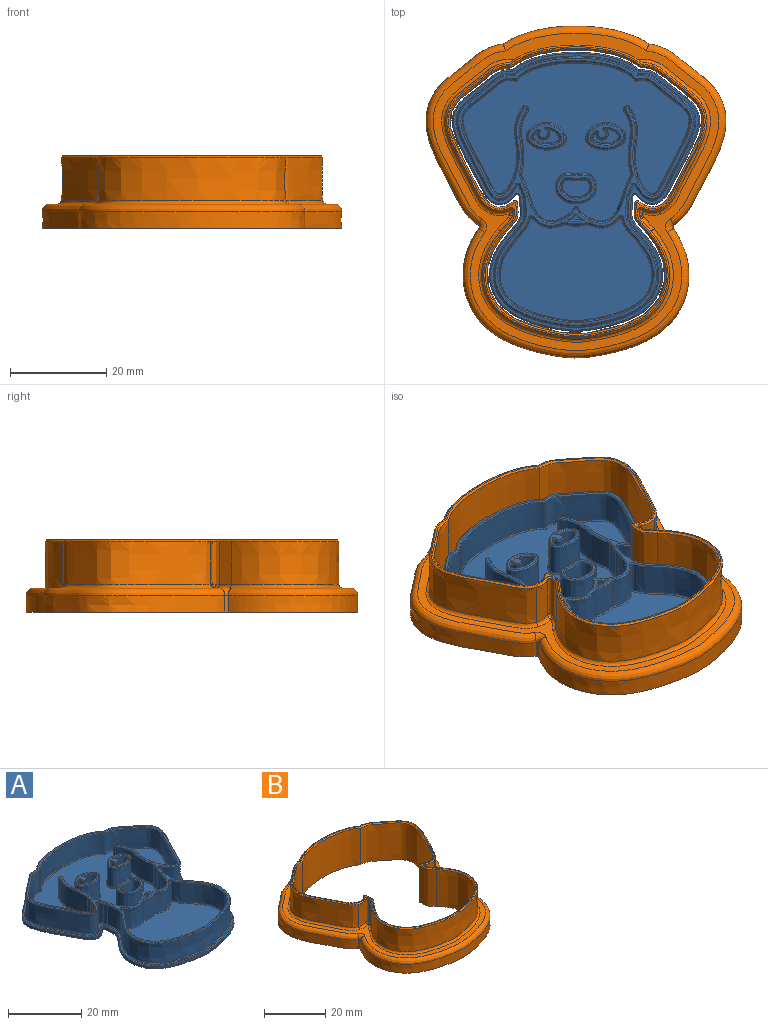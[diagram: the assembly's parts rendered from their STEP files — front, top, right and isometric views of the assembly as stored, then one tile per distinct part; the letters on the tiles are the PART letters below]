
ASSEMBLY  parts=2 mates=1
PART A: 217 faces, bbox 51.8x58.5x8.3 mm
  f0: plane 47x32.89mm, normal (0,0,1), area 914.6mm2, adj f103,f104,f105,f106,f107,f108,f109,f110
  f1: plane 57.65x51.01mm, normal (0,0,1), area 99.7mm2, adj f93,f94,f95,f96,f97,f98,f99,f100
  f2: plane 0.75x0.22mm, normal (0.92,-0.39,0), area 0.2mm2, adj f7,f8,f77,f93
  f3: extruded ~28.07x13.13mm, area 31.7mm2, adj f8,f77,f79,f96
  f4: extruded ~26.17x3.56mm, area 20.7mm2, adj f8,f79,f80,f100
  f5: extruded ~28.07x13.13mm, area 31.7mm2, adj f8,f78,f80,f101
  f6: plane 0.75x0.23mm, normal (-0.92,-0.39,0), area 0.2mm2, adj f7,f8,f78,f97
  f7: extruded ~35.85x28.04mm, area 62.9mm2, adj f2,f6,f8,f95
  f8: plane 58.16x51.5mm, normal (0,0,-1), area 2076.8mm2, adj f2,f3,f4,f5,f6,f7,f77,f78
  f9: extruded ~6.75x1.14mm, area 10.1mm2, adj f10,f47,f49,f215
  f10: extruded ~6.75x2.28mm, area 15.4mm2, adj f9,f47,f49,f216
  f11: extruded ~6.5x4.94mm, area 32.5mm2, adj f12,f44,f147,f199
  f12: extruded ~6.54x6.5mm, area 47.4mm2, adj f11,f65,f149,f201
  f13: extruded ~32.03x21.55mm, area 445.9mm2, adj f65,f66,f148,f198
  f14: extruded ~33.88x27.04mm, area 525.8mm2, adj f15,f45,f138,f166
  f15: extruded ~6.5x1.13mm, area 7.8mm2, adj f14,f16,f136,f168
  f16: plane 6.5x1.24mm, normal (0.92,-0.39,0), area 8.8mm2, adj f15,f74,f134,f167
  f17: extruded ~6.5x0.39mm, area 2.9mm2, adj f18,f74,f131,f163
  f18: extruded ~26.04x12.06mm, area 257.6mm2, adj f17,f70,f133,f161
  f19: extruded ~25.4x6.5mm, area 175.4mm2, adj f70,f73,f137,f157
  f20: extruded ~26.04x12.07mm, area 257.6mm2, adj f21,f73,f141,f156
  f21: extruded ~6.5x0.39mm, area 2.9mm2, adj f20,f67,f143,f158
  f22: plane 6.5x1.24mm, normal (-0.92,-0.39,0), area 8.8mm2, adj f45,f67,f142,f162
  f23: extruded ~13.41x6.5mm, area 89.6mm2, adj f24,f75,f124,f176
  f24: plane 6.5x3.07mm, normal (-0.92,0.39,0), area 21.7mm2, adj f23,f25,f122,f174
  f25: extruded ~6.5x1.35mm, area 9.3mm2, adj f24,f26,f120,f172
  f26: extruded ~7.32x6.5mm, area 68.8mm2, adj f25,f27,f118,f170
  f27: extruded ~6.5x2.18mm, area 18.7mm2, adj f26,f28,f116,f169
  f28: extruded ~6.75x1.66mm, area 7.6mm2, adj f27,f29,f48,f114,f169,f171
  f29: extruded ~6.5x2.23mm, area 19.1mm2, adj f28,f30,f112,f171
  f30: extruded ~7.28x6.5mm, area 68.5mm2, adj f29,f31,f110,f173
  f31: extruded ~6.5x1.35mm, area 9.3mm2, adj f30,f32,f108,f175
  f32: plane 6.5x3.09mm, normal (0.92,0.39,0), area 21.8mm2, adj f31,f33,f106,f177
  f33: extruded ~13.39x6.5mm, area 89.5mm2, adj f32,f69,f104,f179
  f34: plane 6.5x0.17mm, normal (0.56,0.83,0), area 1.3mm2, adj f68,f69,f105,f183
  f35: extruded ~12.37x6.5mm, area 82.8mm2, adj f36,f68,f109,f187
  f36: extruded ~6.5x1.63mm, area 10.9mm2, adj f35,f37,f111,f189
  f37: extruded ~6.5x1.34mm, area 9.3mm2, adj f36,f38,f113,f191
  f38: extruded ~24.06x11.06mm, area 238.1mm2, adj f37,f72,f115,f193
  f39: extruded ~24.57x6.5mm, area 171mm2, adj f71,f72,f119,f194
  f40: extruded ~24.06x11.06mm, area 238mm2, adj f41,f71,f123,f190
  f41: extruded ~6.5x1.33mm, area 9.3mm2, adj f40,f42,f125,f188
  f42: extruded ~6.5x1.62mm, area 10.8mm2, adj f41,f43,f127,f186
  f43: extruded ~12.4x6.5mm, area 83mm2, adj f42,f76,f129,f184
  f44: extruded ~6.5x6.5mm, area 47.1mm2, adj f11,f66,f145,f197
  f45: extruded ~6.5x1.14mm, area 7.9mm2, adj f14,f22,f140,f164
  f46: plane 6.5x0.17mm, normal (-0.56,0.83,0), area 1.3mm2, adj f75,f76,f128,f180
  f47: extruded ~6.75x1.14mm, area 10.1mm2, adj f9,f10,f49,f214
  f48: plane 55.97x49.58mm, normal (0,0,1), area 154.2mm2, adj f28,f155,f156,f157,f158,f159,f160,f161
  f49: plane 2.28x1.05mm, normal (0,0,1), area 1.1mm2, adj f9,f10,f47
  f50: plane 31.57x21.39mm, normal (0,0,1), area 515.5mm2, adj f145,f146,f147,f148,f149,f150
  f51: extruded ~6.5x5.87mm, area 83.3mm2, adj f81,f82,f90,f209
  f52: cylinder r=1.08mm len=6.5mm, axis (0,0,-1), area 33.4mm2, adj f81,f82,f91,f208
  f53: extruded ~7.86x6.5mm, area 134.7mm2, adj f154,f211
  f54: plane 7.73x5.2mm, normal (0,0,1), area 10.7mm2, adj f207,f208,f209,f210,f211
  f55: plane 5.38x2.79mm, normal (0,0,1), area 6.5mm2, adj f90,f91
  f56: extruded ~6.5x5.86mm, area 82mm2, adj f83,f84,f86,f204
  f57: extruded ~7.86x6.5mm, area 134.7mm2, adj f153,f206
  f58: cylinder r=1.08mm len=6.5mm, axis (0,0,-1), area 31.8mm2, adj f83,f84,f87,f203
  f59: plane 7.78x5.2mm, normal (0,0,1), area 11.4mm2, adj f202,f203,f204,f205,f206
  f60: plane 5.38x2.8mm, normal (0,0,1), area 6.7mm2, adj f86,f87
  f61: extruded ~6.5x6.19mm, area 110.4mm2, adj f152,f212
  f62: extruded ~8.19x6.5mm, area 150.2mm2, adj f151,f213
  f63: plane 8.04x5.85mm, normal (0,0,1), area 10.1mm2, adj f212,f213
  f64: plane 5.71x3.47mm, normal (0,0,1), area 16.4mm2, adj f152
  f65: cylinder r=0.4mm len=6.5mm, axis (0,0,-1), area 6mm2, adj f12,f13,f150,f200
  f66: cylinder r=0.4mm len=6.5mm, axis (0,0,-1), area 5.9mm2, adj f13,f44,f146,f196
  f67: cylinder r=0.4mm len=6.5mm, axis (0,0,-1), area 5.9mm2, adj f21,f22,f144,f160
  f68: cylinder r=0.4mm len=6.5mm, axis (0,0,-1), area 4.2mm2, adj f34,f35,f107,f185
  f69: cylinder r=0.4mm len=6.5mm, axis (0,0,-1), area 4mm2, adj f33,f34,f103,f181
  f70: cylinder r=0.4mm len=6.5mm, axis (0,0,-1), area 2.4mm2, adj f18,f19,f135,f159
  f71: cylinder r=0.4mm len=6.5mm, axis (0,0,-1), area 2.9mm2, adj f39,f40,f121,f192
  f72: cylinder r=0.4mm len=6.5mm, axis (0,0,-1), area 2.9mm2, adj f38,f39,f117,f195
  f73: cylinder r=0.4mm len=6.5mm, axis (0,0,-1), area 2.4mm2, adj f19,f20,f139,f155
  f74: cylinder r=0.4mm len=6.5mm, axis (0,0,-1), area 5.9mm2, adj f16,f17,f132,f165
  f75: cylinder r=0.4mm len=6.5mm, axis (0,0,-1), area 4mm2, adj f23,f46,f126,f178
  f76: cylinder r=0.4mm len=6.5mm, axis (0,0,-1), area 4.2mm2, adj f43,f46,f130,f182
  f77: cylinder r=0.4mm len=0.75mm, axis (0,0,-1), area 0.6mm2, adj f2,f3,f8,f94
  f78: cylinder r=0.4mm len=0.75mm, axis (0,0,-1), area 0.6mm2, adj f5,f6,f8,f99
  f79: cylinder r=0.4mm len=0.75mm, axis (0,0,-1), area 0.2mm2, adj f3,f4,f8,f98
  f80: cylinder r=0.4mm len=0.75mm, axis (0,0,-1), area 0.2mm2, adj f4,f5,f8,f102
  f81: cylinder r=0.1mm len=6.5mm, axis (0,0,-1), area 1.7mm2, adj f51,f52,f92,f210
  f82: cylinder r=0.1mm len=6.5mm, axis (0,0,-1), area 1.7mm2, adj f51,f52,f89,f207
  f83: cylinder r=0.1mm len=6.5mm, axis (0,0,-1), area 1.7mm2, adj f56,f58,f88,f205
  f84: cylinder r=0.1mm len=6.5mm, axis (0,0,-1), area 1.7mm2, adj f56,f58,f85,f202
  f85: bspline ~0.65x0.41mm, area 0.1mm2, adj f84,f86,f87
  f86: bspline ~5.88x3.32mm, area 4.6mm2, adj f56,f60,f85,f88
  f87: torus R=1.33mm, axis (0,0,1), area 1.9mm2, adj f58,f60,f85,f88
  f88: bspline ~0.79x0.29mm, area 0.1mm2, adj f83,f86,f87
  f89: bspline ~0.6x0.57mm, area 0.1mm2, adj f82,f90,f91
  f90: bspline ~5.88x3.31mm, area 4.6mm2, adj f51,f55,f89,f92
  f91: torus R=1.33mm, axis (0,0,1), area 2mm2, adj f52,f55,f89,f92
  f92: bspline ~0.83x0.3mm, area 0.1mm2, adj f81,f90,f91
  f93: cylinder r=0.25mm len=0.36mm, axis (-0.39,-0.92,0), area 0.1mm2, adj f1,f2,f94,f95
  f94: torus R=0.65mm, axis (0,0,1), area 0.4mm2, adj f1,f77,f93,f96
  f95: bspline ~36.08x29.88mm, area 32.9mm2, adj f1,f7,f93,f97
  f96: bspline ~28.11x13.67mm, area 16.4mm2, adj f1,f3,f94,f98
  f97: cylinder r=0.25mm len=0.36mm, axis (-0.39,0.92,0), area 0.1mm2, adj f1,f6,f95,f99
  f98: torus R=0.65mm, axis (0,0,1), area 0.2mm2, adj f1,f79,f96,f100
  f99: torus R=0.65mm, axis (0,0,1), area 0.4mm2, adj f1,f78,f97,f101
  f100: bspline ~26.62x3.96mm, area 10.8mm2, adj f1,f4,f98,f102
  f101: bspline ~28.1x13.67mm, area 16.4mm2, adj f1,f5,f99,f102
  f102: torus R=0.65mm, axis (0,0,1), area 0.2mm2, adj f1,f80,f100,f101
  f103: torus R=0.65mm, axis (0,0,1), area 0.3mm2, adj f0,f69,f104,f105
  f104: bspline ~14.22x2.05mm, area 5.4mm2, adj f0,f33,f103,f106
  f105: cylinder r=0.25mm len=0.32mm, axis (0.83,-0.56,0), area 0.1mm2, adj f0,f34,f103,f107
  f106: cylinder r=0.25mm len=3.18mm, axis (0.39,-0.92,0), area 1.3mm2, adj f0,f32,f104,f108
  f107: torus R=0.65mm, axis (0,0,1), area 0.3mm2, adj f0,f68,f105,f109
  f108: bspline ~1.91x0.87mm, area 0.6mm2, adj f0,f31,f106,f110
  f109: bspline ~15.66x2.35mm, area 5mm2, adj f0,f35,f107,f111
  f110: bspline ~8.29x6.32mm, area 4.1mm2, adj f0,f30,f108,f112
  f111: bspline ~2.23x0.77mm, area 0.7mm2, adj f0,f36,f109,f113
  f112: bspline ~6.55x4.18mm, area 1.1mm2, adj f0,f29,f110,f114
  f113: bspline ~1.88x0.92mm, area 0.6mm2, adj f0,f37,f111,f115
  f114: bspline ~1.31x0.91mm, area 0.5mm2, adj f0,f28,f112,f116
  f115: bspline ~24.1x12.37mm, area 14.2mm2, adj f0,f38,f113,f117
  f116: bspline ~2.98x2.35mm, area 1.1mm2, adj f0,f27,f114,f118
  f117: torus R=0.65mm, axis (0,0,1), area 0.2mm2, adj f0,f72,f115,f119
  f118: bspline ~10.84x7.11mm, area 4.1mm2, adj f0,f26,f116,f120
  f119: bspline ~24.99x4.07mm, area 10.3mm2, adj f0,f39,f117,f121
  f120: bspline ~1.91x0.87mm, area 0.6mm2, adj f0,f25,f118,f122
  f121: torus R=0.65mm, axis (0,0,1), area 0.2mm2, adj f0,f71,f119,f123
  f122: cylinder r=0.25mm len=3.17mm, axis (0.39,0.92,0), area 1.3mm2, adj f0,f24,f120,f124
  f123: bspline ~24.1x12.37mm, area 14.2mm2, adj f0,f40,f121,f125
  f124: bspline ~14.22x2.05mm, area 5.4mm2, adj f0,f23,f122,f126
  f125: bspline ~3.52x1.44mm, area 0.6mm2, adj f0,f41,f123,f127
  f126: torus R=0.65mm, axis (0,0,1), area 0.3mm2, adj f0,f75,f124,f128
  f127: bspline ~2.22x0.77mm, area 0.6mm2, adj f0,f42,f125,f129
  f128: cylinder r=0.25mm len=0.32mm, axis (0.83,0.56,0), area 0.1mm2, adj f0,f46,f126,f130
  f129: bspline ~15.69x2.36mm, area 5mm2, adj f0,f43,f127,f130
  f130: torus R=0.65mm, axis (0,0,1), area 0.3mm2, adj f0,f76,f128,f129
  f131: bspline ~0.76x0.57mm, area 0.2mm2, adj f1,f17,f132,f133
  f132: torus R=0.15mm, axis (0,0,1), area 0.3mm2, adj f1,f74,f131,f134
  f133: bspline ~26.6x14.45mm, area 15.7mm2, adj f1,f18,f131,f135
  f134: cylinder r=0.25mm len=1.34mm, axis (-0.39,-0.92,0), area 0.5mm2, adj f1,f16,f132,f136
  f135: torus R=0.15mm, axis (0,0,1), area 0.1mm2, adj f1,f70,f133,f137
  f136: bspline ~1.58x0.77mm, area 0.5mm2, adj f1,f15,f134,f138
  f137: bspline ~26.07x3.99mm, area 10.7mm2, adj f1,f19,f135,f139
  f138: bspline ~34.59x28.02mm, area 31.8mm2, adj f1,f14,f136,f140
  f139: torus R=0.15mm, axis (0,0,1), area 0.1mm2, adj f1,f73,f137,f141
  f140: bspline ~1.6x0.78mm, area 0.5mm2, adj f1,f45,f138,f142
  f141: bspline ~26.6x14.46mm, area 15.7mm2, adj f1,f20,f139,f143
  f142: cylinder r=0.25mm len=1.34mm, axis (-0.39,0.92,0), area 0.5mm2, adj f1,f22,f140,f144
  f143: bspline ~0.76x0.56mm, area 0.2mm2, adj f1,f21,f141,f144
  f144: torus R=0.15mm, axis (0,0,1), area 0.3mm2, adj f1,f67,f142,f143
  f145: bspline ~7.37x2.68mm, area 2.9mm2, adj f44,f50,f146,f147
  f146: torus R=0.15mm, axis (0,0,1), area 0.3mm2, adj f50,f66,f145,f148
  f147: bspline ~7.43x1.26mm, area 1.9mm2, adj f11,f50,f145,f149
  f148: bspline ~32.07x21.97mm, area 26.8mm2, adj f13,f50,f146,f150
  f149: bspline ~7.36x2.69mm, area 2.9mm2, adj f12,f50,f147,f150
  f150: torus R=0.15mm, axis (0,0,1), area 0.3mm2, adj f50,f65,f148,f149
  f151: bspline ~8.72x6.47mm, area 9.3mm2, adj f0,f62
  f152: bspline ~6.21x3.97mm, area 6.4mm2, adj f61,f64
  f153: bspline ~8.38x5.82mm, area 8.4mm2, adj f0,f57
  f154: bspline ~8.38x5.82mm, area 8.4mm2, adj f0,f53
  f155: cone r=0.65mm half-angle=45deg, axis (0,0,1), area 0.2mm2, adj f48,f73,f156,f157
  f156: bspline ~26.21x12.13mm, area 13.9mm2, adj f20,f48,f155,f158
  f157: bspline ~25.4x3.76mm, area 9.4mm2, adj f19,f48,f155,f159
  f158: bspline ~0.5x0.43mm, area 0.2mm2, adj f21,f48,f156,f160
  f159: cone r=0.65mm half-angle=45deg, axis (0,0,1), area 0.2mm2, adj f48,f70,f157,f161
  f160: cone r=0.65mm half-angle=45deg, axis (0,0,1), area 0.4mm2, adj f48,f67,f158,f162
  f161: bspline ~26.21x12.14mm, area 13.8mm2, adj f18,f48,f159,f163
  f162: plane 1.34x0.76mm, normal (-0.65,-0.28,0.71), area 0.5mm2, adj f22,f48,f160,f164
  f163: bspline ~0.5x0.43mm, area 0.2mm2, adj f17,f48,f161,f165
  f164: bspline ~1.28x0.65mm, area 0.4mm2, adj f45,f48,f162,f166
  f165: cone r=0.65mm half-angle=45deg, axis (0,0,1), area 0.4mm2, adj f48,f74,f163,f167
  f166: bspline ~34.09x29.26mm, area 28.4mm2, adj f14,f48,f164,f168
  f167: plane 1.34x0.76mm, normal (0.65,-0.28,0.71), area 0.5mm2, adj f16,f48,f165,f168
  f168: bspline ~1.25x0.64mm, area 0.4mm2, adj f15,f48,f166,f167
  f169: bspline ~2.39x2.05mm, area 0.9mm2, adj f27,f28,f48,f170
  f170: bspline ~7.68x5.73mm, area 3.8mm2, adj f26,f48,f169,f172
  f171: bspline ~2.52x2.2mm, area 0.9mm2, adj f28,f29,f48,f173
  f172: bspline ~1.42x0.7mm, area 0.5mm2, adj f25,f48,f170,f174
  f173: bspline ~7.63x5.73mm, area 3.8mm2, adj f30,f48,f171,f175
  f174: plane 3.17x1.58mm, normal (-0.65,0.28,0.71), area 1.2mm2, adj f24,f48,f172,f176
  f175: bspline ~1.42x0.7mm, area 0.5mm2, adj f31,f48,f173,f177
  f176: bspline ~14.31x1.92mm, area 4.9mm2, adj f23,f48,f174,f178
  f177: plane 3.19x1.58mm, normal (0.65,0.28,0.71), area 1.2mm2, adj f32,f48,f175,f179
  f178: cone r=0.15mm half-angle=45deg, axis (0,0,-1), area 0.2mm2, adj f48,f75,f176,f180
  f179: bspline ~14.29x1.91mm, area 4.9mm2, adj f33,f48,f177,f181
  f180: plane 0.32x0.31mm, normal (-0.4,0.58,0.71), area 0.1mm2, adj f46,f48,f178,f182
  f181: cone r=0.15mm half-angle=45deg, axis (0,0,-1), area 0.2mm2, adj f48,f69,f179,f183
  f182: cone r=0.15mm half-angle=45deg, axis (0,0,-1), area 0.2mm2, adj f48,f76,f180,f184
  f183: plane 0.32x0.31mm, normal (0.4,0.58,0.71), area 0.1mm2, adj f34,f48,f181,f185
  f184: bspline ~12.44x1.86mm, area 4.5mm2, adj f43,f48,f182,f186
  f185: cone r=0.15mm half-angle=45deg, axis (0,0,-1), area 0.2mm2, adj f48,f68,f183,f187
  f186: bspline ~1.69x0.64mm, area 0.6mm2, adj f42,f48,f184,f188
  f187: bspline ~12.41x1.83mm, area 4.5mm2, adj f35,f48,f185,f189
  f188: bspline ~1.44x0.75mm, area 0.5mm2, adj f41,f48,f186,f190
  f189: bspline ~1.71x0.64mm, area 0.6mm2, adj f36,f48,f187,f191
  f190: bspline ~24.73x11.44mm, area 13.1mm2, adj f40,f48,f188,f192
  f191: bspline ~1.45x0.75mm, area 0.5mm2, adj f37,f48,f189,f193
  f192: cone r=0.15mm half-angle=45deg, axis (0,0,-1), area 0.1mm2, adj f48,f71,f190,f194
  f193: bspline ~24.73x11.45mm, area 13.1mm2, adj f38,f48,f191,f195
  f194: bspline ~24.96x3.88mm, area 9.4mm2, adj f39,f48,f192,f195
  f195: cone r=0.15mm half-angle=45deg, axis (0,0,-1), area 0.1mm2, adj f48,f72,f193,f194
  f196: cone r=0.65mm half-angle=45deg, axis (0,0,1), area 0.4mm2, adj f48,f66,f197,f198
  f197: bspline ~6.9x2.16mm, area 2.5mm2, adj f44,f48,f196,f199
  f198: bspline ~32.63x21.85mm, area 24.4mm2, adj f13,f48,f196,f200
  f199: bspline ~5.61x0.85mm, area 1.8mm2, adj f11,f48,f197,f201
  f200: cone r=0.65mm half-angle=45deg, axis (0,0,1), area 0.4mm2, adj f48,f65,f198,f201
  f201: bspline ~6.95x2.18mm, area 2.5mm2, adj f12,f48,f199,f200
  f202: cone r=0.35mm half-angle=45deg, axis (0,0,1), area 0.2mm2, adj f59,f84,f203,f204
  f203: cone r=0.83mm half-angle=45deg, axis (0,0,-1), area 1.5mm2, adj f58,f59,f202,f205
  f204: bspline ~6.44x3.88mm, area 4.7mm2, adj f56,f59,f202,f205
  f205: cone r=0.35mm half-angle=45deg, axis (0,0,1), area 0.2mm2, adj f59,f83,f203,f204
  f206: bspline ~8.02x5.41mm, area 7.1mm2, adj f57,f59
  f207: cone r=0.35mm half-angle=45deg, axis (0,0,1), area 0.2mm2, adj f54,f82,f208,f209
  f208: cone r=0.83mm half-angle=45deg, axis (0,0,-1), area 1.6mm2, adj f52,f54,f207,f210
  f209: bspline ~6.44x3.87mm, area 4.8mm2, adj f51,f54,f207,f210
  f210: cone r=0.35mm half-angle=45deg, axis (0,0,1), area 0.2mm2, adj f54,f81,f208,f209
  f211: bspline ~8.02x5.4mm, area 7.1mm2, adj f53,f54
  f212: bspline ~6.72x4.52mm, area 6.2mm2, adj f61,f63
  f213: bspline ~8.2x5.96mm, area 7.9mm2, adj f62,f63
  f214: bspline ~2.01x1.69mm, area 0.7mm2, adj f47,f48,f215,f216
  f215: bspline ~2x1.69mm, area 0.7mm2, adj f9,f48,f214,f216
  f216: bspline ~3.65x0.43mm, area 1.1mm2, adj f10,f48,f214,f215
PART B: 78 faces, bbox 63x69.6x15.5 mm
  f0: extruded ~8.9x3.47mm, area 31.8mm2, adj f7,f29,f33,f76
  f1: extruded ~8.9x2.54mm, area 29.9mm2, adj f2,f17,f38,f71
  f2: extruded ~39.05x22.4mm, area 642.2mm2, adj f1,f3,f40,f70
  f3: extruded ~8.9x2.48mm, area 29.1mm2, adj f2,f18,f42,f69
  f4: extruded ~8.9x3.52mm, area 32.3mm2, adj f5,f31,f41,f64
  f5: extruded ~30.86x13.5mm, area 364.7mm2, adj f4,f6,f39,f63
  f6: extruded ~27.5x9.65mm, area 278.5mm2, adj f5,f7,f26,f37,f63,f77
  f7: extruded ~30.86x13.5mm, area 364.9mm2, adj f0,f6,f35,f77
  f8: extruded ~14.65x0.18mm, area 3.6mm2, adj f9,f21,f30,f45
  f9: extruded ~29.06x14.65mm, area 624.1mm2, adj f8,f10,f21,f47
  f10: extruded ~26.78x14.65mm, area 414.7mm2, adj f9,f11,f21,f49
  f11: extruded ~29.06x14.65mm, area 624.5mm2, adj f10,f12,f21,f51
  f12: extruded ~14.65x0.18mm, area 3.6mm2, adj f11,f21,f32,f53
  f13: extruded ~14.65x0.24mm, area 3.6mm2, adj f14,f21,f32,f56
  f14: extruded ~14.65x5.51mm, area 91.2mm2, adj f13,f15,f21,f54
  f15: extruded ~37.04x21.56mm, area 1023.2mm2, adj f14,f16,f21,f52
  f16: extruded ~14.65x5.48mm, area 90.7mm2, adj f15,f19,f21,f50
  f17: extruded ~8.9x1.5mm, area 14.2mm2, adj f1,f29,f36,f72,f73,f74
  f18: extruded ~8.9x1.57mm, area 15.2mm2, adj f3,f31,f44,f66,f67,f68
  f19: extruded ~14.65x0.24mm, area 3.5mm2, adj f16,f21,f30,f48
  f20: plane 60.94x54.48mm, normal (0,0,1), area 51.6mm2, adj f33,f34,f35,f36,f37,f38,f39,f40
  f21: plane 69.15x62.5mm, normal (0,0,-1), area 1040.6mm2, adj f8,f9,f10,f11,f12,f13,f14,f15
  f22: extruded ~47.07x27mm, area 298.9mm2, adj f21,f27,f28,f60
  f23: extruded ~37.7x16.07mm, area 171.1mm2, adj f21,f24,f27,f57
  f24: extruded ~30.36x3.74mm, area 110.9mm2, adj f21,f23,f25,f59
  f25: extruded ~37.7x16.07mm, area 171mm2, adj f21,f24,f28,f61
  f26: plane 66.15x59.51mm, normal (0,0,1), area 388.2mm2, adj f6,f57,f58,f59,f60,f61,f62,f63
  f27: cylinder r=0.5mm len=3.5mm, axis (0,0,-1), area 2.8mm2, adj f21,f22,f23,f58
  f28: cylinder r=0.5mm len=3.5mm, axis (0,0,-1), area 2.8mm2, adj f21,f22,f25,f62
  f29: cylinder r=0.5mm len=8.9mm, axis (0,0,-1), area 8.9mm2, adj f0,f17,f34,f75
  f30: cylinder r=0.5mm len=14.65mm, axis (0,0,-1), area 16.3mm2, adj f8,f19,f21,f46
  f31: cylinder r=0.5mm len=8.9mm, axis (0,0,-1), area 9mm2, adj f4,f18,f43,f65
  f32: cylinder r=0.5mm len=14.65mm, axis (0,0,-1), area 16.2mm2, adj f12,f13,f21,f55
  f33: bspline ~3.47x0.96mm, area 1.7mm2, adj f0,f20,f34,f35
  f34: cone r=0.85mm half-angle=45deg, axis (0,0,1), area 0.7mm2, adj f20,f29,f33,f36
  f35: bspline ~30.88x14.78mm, area 20.1mm2, adj f7,f20,f33,f37
  f36: bspline ~1.72x0.74mm, area 0.8mm2, adj f17,f20,f34,f38
  f37: bspline ~27.69x4mm, area 14.3mm2, adj f6,f20,f35,f39
  f38: bspline ~2.76x2.49mm, area 1.7mm2, adj f1,f20,f36,f40
  f39: bspline ~30.87x14.81mm, area 20.1mm2, adj f5,f20,f37,f41
  f40: bspline ~39.11x22.41mm, area 35.6mm2, adj f2,f20,f38,f42
  f41: bspline ~3.52x0.98mm, area 1.7mm2, adj f4,f20,f39,f43
  f42: bspline ~2.71x2.4mm, area 1.6mm2, adj f3,f20,f40,f44
  f43: cone r=0.85mm half-angle=45deg, axis (0,0,1), area 0.7mm2, adj f20,f31,f41,f44
  f44: bspline ~1.79x0.85mm, area 0.9mm2, adj f18,f20,f42,f43
  f45: bspline ~0.43x0.42mm, area 0.1mm2, adj f8,f20,f46,f47
  f46: cone r=0.15mm half-angle=45deg, axis (0,0,-1), area 0.4mm2, adj f20,f30,f45,f48
  f47: bspline ~29.86x13.62mm, area 21.4mm2, adj f9,f20,f45,f49
  f48: bspline ~0.37x0.35mm, area 0.1mm2, adj f19,f20,f46,f50
  f49: bspline ~29.38x4.99mm, area 14.1mm2, adj f10,f20,f47,f51
  f50: bspline ~5.48x2.4mm, area 3mm2, adj f16,f20,f48,f52
  f51: bspline ~29.86x13.66mm, area 21.4mm2, adj f11,f20,f49,f53
  f52: bspline ~37.89x22.15mm, area 35.1mm2, adj f15,f20,f50,f54
  f53: bspline ~0.43x0.42mm, area 0.1mm2, adj f12,f20,f51,f55
  f54: bspline ~5.51x2.44mm, area 3mm2, adj f14,f20,f52,f56
  f55: cone r=0.15mm half-angle=45deg, axis (0,0,-1), area 0.4mm2, adj f20,f32,f53,f56
  f56: bspline ~0.37x0.35mm, area 0.1mm2, adj f13,f20,f54,f55
  f57: bspline ~38.14x16.98mm, area 112.4mm2, adj f23,f26,f58,f59
  f58: torus R=2mm, axis (0,0,-1), area 4mm2, adj f26,f27,f57,f60
  f59: bspline ~32.28x5.83mm, area 74mm2, adj f24,f26,f57,f61
  f60: bspline ~47.08x27.48mm, area 196.5mm2, adj f22,f26,f58,f62
  f61: bspline ~37.99x16.74mm, area 112.3mm2, adj f25,f26,f59,f62
  f62: torus R=2mm, axis (0,0,-1), area 4mm2, adj f26,f28,f60,f61
  f63: bspline ~36.38x22.57mm, area 49.8mm2, adj f5,f6,f26,f64
  f64: bspline ~5.44x1.39mm, area 4.3mm2, adj f4,f26,f63,f65
  f65: bspline ~0.89x0.76mm, area 0.6mm2, adj f31,f64,f66
  f66: bspline ~1.71x0.85mm, area 0.7mm2, adj f18,f26,f65,f67
  f67: bspline ~0.75x0.72mm, area 0mm2, adj f18,f66,f68
  f68: bspline ~1.13x1.11mm, area 0.8mm2, adj f18,f26,f67,f69
  f69: bspline ~3.83x3.41mm, area 3.8mm2, adj f3,f26,f68,f70
  f70: bspline ~40.58x33.84mm, area 86.9mm2, adj f2,f26,f69,f71
  f71: bspline ~3.96x3.56mm, area 3.9mm2, adj f1,f26,f70,f72
  f72: bspline ~1.08x1.03mm, area 0.6mm2, adj f17,f26,f71,f73
  f73: bspline ~0.75x0.73mm, area 0.1mm2, adj f17,f72,f74
  f74: bspline ~1.37x0.83mm, area 0.8mm2, adj f17,f26,f73,f75
  f75: bspline ~1.17x0.8mm, area 0.6mm2, adj f29,f74,f76
  f76: bspline ~5.48x1.38mm, area 4.2mm2, adj f0,f26,f75,f77
  f77: bspline ~36.35x22.64mm, area 49.9mm2, adj f6,f7,f26,f76
PLACE A t=(-20.56,-8.13,-2.21)mm
PLACE B t=(-20.55,-8.17,-2.21)mm
MATE fastened A.f8 <-> B.f21  axis (0,0,-1) through (-20.56,-4.76,-2.21)mm
